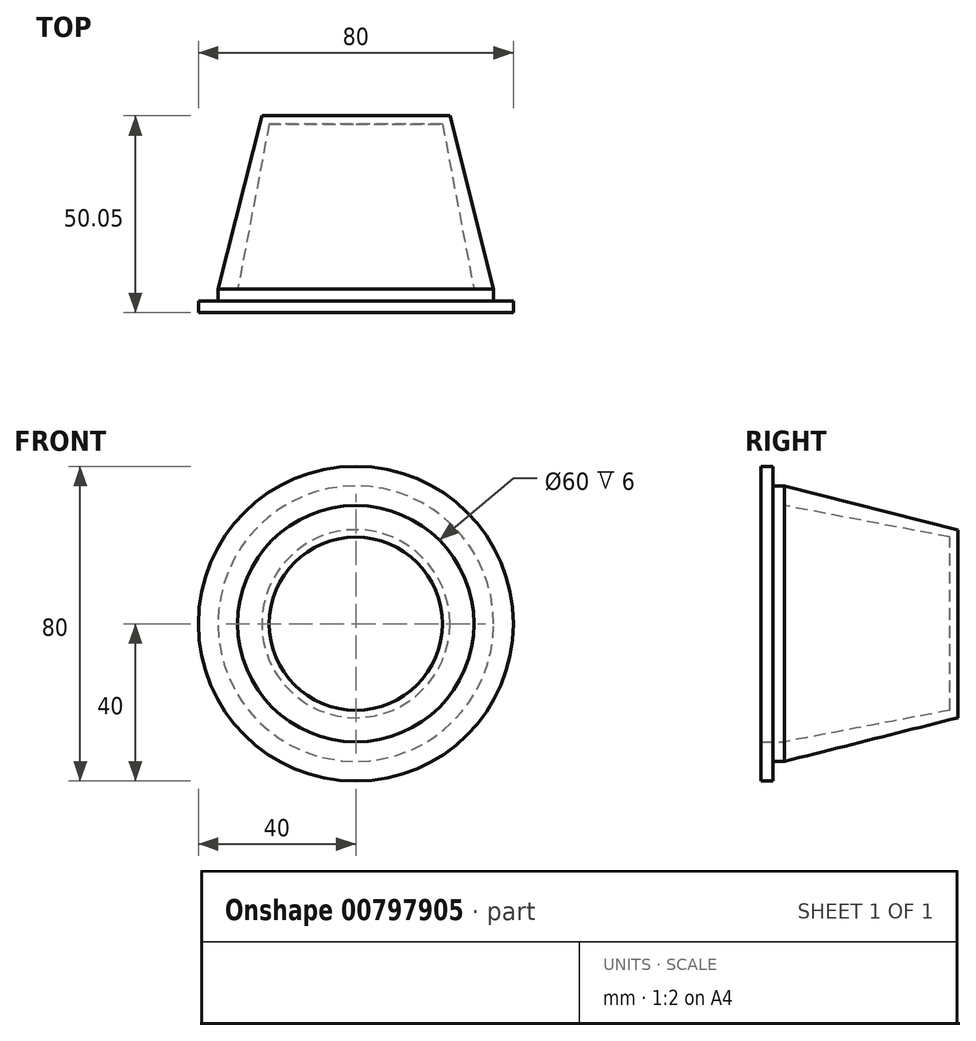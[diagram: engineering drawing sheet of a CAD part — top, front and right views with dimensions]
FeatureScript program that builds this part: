
annotation { "Feature Type Name" : "Feature", "Feature Type Description" : "" }
export const myFeature = defineFeature(function(context is Context, id is Id, definition is map)
    precondition{}
    {
        {
            var Q0;
            Q0=qCreatedBy(makeId("Front.planeOp"),FACE);
            var sketch = newSketch(context, id + "F0", { "sketchPlane" : qUnion([Q0])});
            skCircle(sketch, "E0", {"center": v(0, 0) * mm, "radius": 40 * mm});
            skCircle(sketch, "E1", {"center": v(0, 0) * mm, "radius": 30 * mm});
            skSolve(sketch);
        }
        {
            var Q0;
            Q0 = qSketchRegion(id + "F0", true);
            extrude(context, id + "F1", {"entities" : qUnion([Q0]), "depth" : 3 * mm, "offsetDistance" : 25 * mm});
        }
        {
            var Q0;
            Q0=qCreatedBy(makeId("Front.planeOp"),FACE);
            var sketch = newSketch(context, id + "F2", { "sketchPlane" : qUnion([Q0])});
            skCircle(sketch, "E2", {"center": v(0, 0) * mm, "radius": 30 * mm});
            skCircle(sketch, "E3", {"center": v(0, 0) * mm, "radius": 35 * mm});
            skSolve(sketch);
        }
        {
            var Q0;
            Q0 = qSketchRegion(id + "F2", true);
            extrude(context, id + "F3", {"entities" : qUnion([Q0]), "operationType" : NewBodyOperationType.ADD, "oppositeDirection" : true, "depth" : 3 * mm, "offsetDistance" : 25 * mm});
        }
        {
            var Q0;
            Q0=qCreatedBy(makeId("Front.planeOp"),FACE);
            cPlane(context, id + "F4", {"entities" : qUnion([Q0]), "cplaneType" : CPlaneType.OFFSET, "offset" : 47.05 * mm, "oppositeDirection" : true, "width" : 150 * mm, "height" : 150 * mm});
        }
        {
            var Q0;
            Q0=qCreatedBy(id+"F4.planeOp",FACE);
            var sketch = newSketch(context, id + "F5", { "sketchPlane" : qUnion([Q0])});
            skCircle(sketch, "E4", {"center": v(0, 0) * mm, "radius": 23.87 * mm});
            skSolve(sketch);
        }
        {
            var Q0;
            Q0=makeQuery(id+"F3.opExtrude","CAP_FACE",FACE,{"disambiguationData":[OSD([sQuery(id+"F2.wireOp",EDGE,"E2"),sQuery(id+"F2.wireOp",EDGE,"E3")])],"isStart":false});
            var sketch = newSketch(context, id + "F6", { "sketchPlane" : qUnion([Q0])});
            skCircle(sketch, "E5", {"center": v(0, 0) * mm, "radius": 35 * mm});
            skSolve(sketch);
        }
        {
            var Q1;
            Q1 = qSketchRegion(id + "F5", true);
            var Q2;
            Q2 = qSketchRegion(id + "F6", true);
            loft(context, id + "F7", {"operationType" : NewBodyOperationType.ADD, "sheetProfilesArray" : [{ "sheetProfileEntities" : qUnion([Q1]) }, { "sheetProfileEntities" : qUnion([Q2]) }]});
        }
        {
            var Q0;
            Q0=qCreatedBy(makeId("Front.planeOp"),FACE);
            cPlane(context, id + "F8", {"entities" : qUnion([Q0]), "cplaneType" : CPlaneType.OFFSET, "offset" : 45 * mm, "oppositeDirection" : true, "width" : 150 * mm, "height" : 150 * mm});
        }
        {
            var Q0;
            Q0=qCreatedBy(id+"F8.planeOp",FACE);
            var sketch = newSketch(context, id + "F9", { "sketchPlane" : qUnion([Q0])});
            skCircle(sketch, "E6", {"center": v(0, 0) * mm, "radius": 22 * mm});
            skSolve(sketch);
        }
        {
            var Q0;
            Q0=makeQuery(id+"F7.opLoft","CAP_FACE",FACE,{"disambiguationData":[OSD([makeQuery(id+"F6.imprint","IMPRINT",FACE,{"disambiguationData":[TD([[makeQuery(id+"F6.imprint","IMPRINT",EDGE,{"derivedFrom":makeQuery(id+"F3.opExtrude","CAP_EDGE",EDGE,{"disambiguationData":[OSD([sQuery(id+"F2.wireOp",EDGE,"E2")])],"isStart":false})}),-1.0]])]})])],"isStart":true});
            var sketch = newSketch(context, id + "F10", { "sketchPlane" : qUnion([Q0])});
            skCircle(sketch, "E7", {"center": v(0, 0) * mm, "radius": 30 * mm});
            skSolve(sketch);
        }
        {
            var Q1;
            Q1 = qSketchRegion(id + "F9", true);
            var Q2;
            Q2 = qSketchRegion(id + "F10", true);
            loft(context, id + "F11", {"operationType" : NewBodyOperationType.REMOVE, "sheetProfilesArray" : [{ "sheetProfileEntities" : qUnion([Q1]) }, { "sheetProfileEntities" : qUnion([Q2]) }]});
        }
    });
